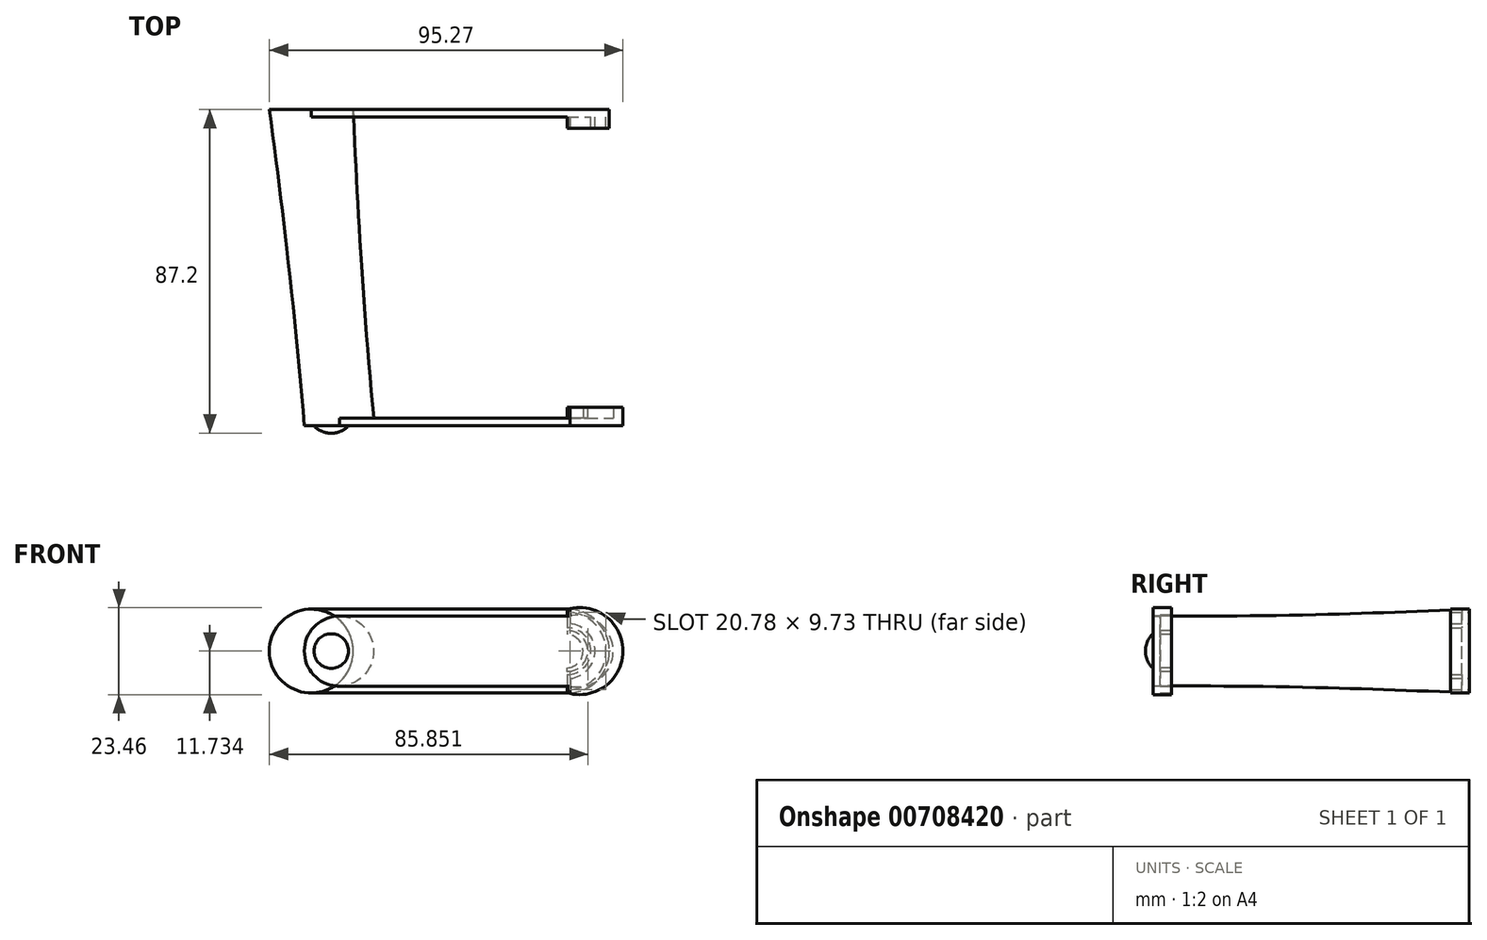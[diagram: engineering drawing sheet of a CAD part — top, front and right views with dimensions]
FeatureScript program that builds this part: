
annotation { "Feature Type Name" : "Feature", "Feature Type Description" : "" }
export const myFeature = defineFeature(function(context is Context, id is Id, definition is map)
    precondition{}
    {
        {
            var Q0;
            Q0=qCreatedBy(makeId("Front.planeOp"),FACE);
            var sketch = newSketch(context, id + "F0", { "sketchPlane" : qUnion([Q0])});
            skCircle(sketch, "E0", {"center": v(0, 0) * mm, "radius": 11.3 * mm});
            skLineSegment(sketch, "E1", {"start": v(0, 11.3) * mm, "end": v(69, 11.3) * mm});
            skLineSegment(sketch, "E2", {"start": v(0, -11.3) * mm, "end": v(69, -11.3) * mm});
            skLineSegment(sketch, "E3", {"start": v(69, 11.3) * mm, "end": v(69, 6.3) * mm});
            skLineSegment(sketch, "E4", {"start": v(69, -6.3) * mm, "end": v(69, -11.3) * mm});
            skArc(sketch, "E5", {"start": v(69, -11.3) * mm, "mid": v(80.3, 0) * mm, "end": v(69, 11.3) * mm});
            skArc(sketch, "E6", {"start": v(69, -6.3) * mm, "mid": v(75.3, 0) * mm, "end": v(69, 6.3) * mm});
            skArc(sketch, "E7", {"start": v(69.69, 10.4) * mm, "mid": v(79.41, 0.06) * mm, "end": v(69.8, -10.38) * mm});
            skArc(sketch, "E8", {"start": v(69.69, 7.4) * mm, "mid": v(76.42, 0.05) * mm, "end": v(69.78, -7.38) * mm});
            skLineSegment(sketch, "E9", {"start": v(69.69, 10.4) * mm, "end": v(69.69, 7.4) * mm});
            skLineSegment(sketch, "E10", {"start": v(69.78, -7.38) * mm, "end": v(69.8, -10.38) * mm});
            skSolve(sketch);
        }
        {
            var Q0;
            Q0=qCreatedBy(makeId("Front.planeOp"),FACE);
            cPlane(context, id + "F1", {"entities" : qUnion([Q0]), "cplaneType" : CPlaneType.OFFSET, "offset" : 85.2 * mm, "width" : 150 * mm, "height" : 150 * mm});
        }
        {
            var Q0;
            Q0=qCreatedBy(id+"F1.planeOp",FACE);
            var sketch = newSketch(context, id + "F2", { "sketchPlane" : qUnion([Q0])});
            skCircle(sketch, "E11", {"center": v(7.55, 0) * mm, "radius": 9.45 * mm});
            skSolve(sketch);
        }
        {
            var Q0;
            Q0=makeQuery(id+"F2.imprint","IMPRINT",FACE,{"disambiguationData":[TD([[makeQuery(id+"F2.imprint","IMPRINT",EDGE,{"derivedFrom":sQuery(id+"F2.wireOp",EDGE,"E11")}),1.0]])]});
            var Q1;
            {var subQ0=sQuery(id+"F0.wireOp",EDGE,"E0");var subQ1=makeQuery(id+"F0.imprint","INTERSECT",VERTEX,{"derivedFrom":[subQ0,sQuery(id+"F0.wireOp",EDGE,"E1")]});Q1=makeQuery(id+"F0.imprint","IMPRINT",FACE,{"disambiguationData":[TD([[makeQuery(id+"F0.imprint","IMPRINT",EDGE,{"disambiguationData":[TD([[subQ1,-1.0]])],"derivedFrom":subQ0}),1.0]])]});}
            loft(context, id + "F3", {"sheetProfilesArray" : [{ "sheetProfileEntities" : qUnion([Q0]) }, { "sheetProfileEntities" : qUnion([Q1]) }]});
        }
        {
            var Q0;
            {var subQ1=sQuery(id+"F0.wireOp",EDGE,"E1");Q0=makeQuery(id+"F0.imprint","IMPRINT",FACE,{"disambiguationData":[TD([[makeQuery(id+"F0.imprint","IMPRINT",EDGE,{"derivedFrom":subQ1}),-1.0]])]});}
            var Q1;
            Q1 = qSketchRegion(id + "F6", true);
            extrude(context, id + "F4", {"entities" : qUnion([Q0, Q1]), "depth" : 2 * mm, "offsetDistance" : 25 * mm});
        }
        {
            var Q0;
            Q0=makeQuery(id+"F0.imprint","IMPRINT",FACE,{"disambiguationData":[TD([[makeQuery(id+"F0.imprint","IMPRINT",EDGE,{"derivedFrom":sQuery(id+"F0.wireOp",EDGE,"E3")}),1.0]])]});
            extrude(context, id + "F5", {"entities" : qUnion([Q0]), "operationType" : NewBodyOperationType.ADD, "depth" : 5 * mm, "offsetDistance" : 25 * mm});
        }
        {
            var Q0;
            Q0=qCreatedBy(id+"F1.planeOp",FACE);
            var sketch = newSketch(context, id + "F6", { "sketchPlane" : qUnion([Q0])});
            skLineSegment(sketch, "E12.bottom", {"start": v(7.55, -9.45) * mm, "end": v(69.67, -9.45) * mm});
            skLineSegment(sketch, "E12.top", {"start": v(7.55, 9.45) * mm, "end": v(69.67, 9.45) * mm});
            skLineSegment(sketch, "E12.left", {"start": v(7.55, -9.45) * mm, "end": v(7.55, 9.45) * mm});
            skArc(sketch, "E13", {"start": v(68.95, -5.5) * mm, "mid": v(74.45, 0) * mm, "end": v(68.95, 5.5) * mm});
            skLineSegment(sketch, "E14", {"start": v(69.67, 9.45) * mm, "end": v(69.67, 11.45) * mm});
            skLineSegment(sketch, "E15", {"start": v(69.67, -9.45) * mm, "end": v(69.67, -11.45) * mm});
            skArc(sketch, "E16", {"start": v(69.67, -11.45) * mm, "mid": v(83.97, 0) * mm, "end": v(69.67, 11.45) * mm});
            skLineSegment(sketch, "E17", {"start": v(68.95, -5.5) * mm, "end": v(68.95, -4.5) * mm});
            skLineSegment(sketch, "E18", {"start": v(68.95, 5.5) * mm, "end": v(68.95, 4.5) * mm});
            skArc(sketch, "E19", {"start": v(68.95, -4.5) * mm, "mid": v(73.2, 0) * mm, "end": v(68.95, 4.5) * mm});
            skArc(sketch, "E20", {"start": v(69.67, -9.45) * mm, "mid": v(81.33, 0) * mm, "end": v(69.67, 9.45) * mm});
            skSolve(sketch);
        }
        {
            var Q0;
            Q0=makeQuery(id+"F6.imprint","IMPRINT",FACE,{"disambiguationData":[TD([[makeQuery(id+"F6.imprint","IMPRINT",EDGE,{"derivedFrom":sQuery(id+"F6.wireOp",EDGE,"E12.bottom")}),1.0]])]});
            extrude(context, id + "F7", {"entities" : qUnion([Q0]), "operationType" : NewBodyOperationType.ADD, "oppositeDirection" : true, "depth" : 2 * mm, "offsetDistance" : 25 * mm});
        }
        {
            var Q0;
            Q0=qCreatedBy(id+"F1.planeOp",FACE);
            var sketch = newSketch(context, id + "F8", { "sketchPlane" : qUnion([Q0])});
            skCircle(sketch, "E21", {"center": v(5.37, 0) * mm, "radius": 4.65 * mm});
            skSolve(sketch);
        }
        {
            var Q0;
            Q0 = qSketchRegion(id + "F8", true);
            extrude(context, id + "F9", {"entities" : qUnion([Q0]), "operationType" : NewBodyOperationType.ADD, "depth" : 2 * mm, "offsetDistance" : 25 * mm});
        }
        {
            var Q0;
            Q0=makeQuery(id+"F9.opExtrude","CAP_FACE",FACE,{"disambiguationData":[OSD([sQuery(id+"F8.wireOp",EDGE,"E21")])],"isStart":false});
            fillet(context, id + "F10", {"entities" : qUnion([Q0]), "radius" : 6 * mm, "tangentPropagation" : true, "allowEdgeOverflow" : false});
        }
        {
            var Q0;
            {var subQ0=sQuery(id+"F6.wireOp",EDGE,"E13");Q0=makeQuery(id+"F6.imprint","IMPRINT",FACE,{"disambiguationData":[TD([[makeQuery(id+"F6.imprint","IMPRINT",EDGE,{"derivedFrom":subQ0}),1.0]])]});}
            extrude(context, id + "F11", {"entities" : qUnion([Q0]), "operationType" : NewBodyOperationType.ADD, "oppositeDirection" : true, "depth" : 2 * mm, "offsetDistance" : 25 * mm});
        }
        {
            var Q0;
            Q0=makeQuery(id+"F0.imprint","IMPRINT",FACE,{"disambiguationData":[TD([[makeQuery(id+"F0.imprint","IMPRINT",EDGE,{"derivedFrom":sQuery(id+"F0.wireOp",EDGE,"E7")}),-1.0]])]});
            extrude(context, id + "F12", {"entities" : qUnion([Q0]), "operationType" : NewBodyOperationType.ADD, "depth" : 2 * mm, "offsetDistance" : 25 * mm});
        }
        {
            var Q0;
            Q0=makeQuery(id+"F0.imprint","IMPRINT",FACE,{"disambiguationData":[TD([[makeQuery(id+"F0.imprint","IMPRINT",EDGE,{"derivedFrom":sQuery(id+"F0.wireOp",EDGE,"E7")}),-1.0]])]});
            extrude(context, id + "F13", {"entities" : qUnion([Q0]), "operationType" : NewBodyOperationType.ADD, "depth" : 3 * mm, "offsetDistance" : 25 * mm});
        }
        {
            var Q0;
            Q0=makeQuery(id+"F6.imprint","IMPRINT",FACE,{"disambiguationData":[TD([[makeQuery(id+"F6.imprint","IMPRINT",EDGE,{"derivedFrom":sQuery(id+"F6.wireOp",EDGE,"E14")}),-1.0]])]});
            extrude(context, id + "F14", {"entities" : qUnion([Q0]), "operationType" : NewBodyOperationType.ADD, "oppositeDirection" : true, "depth" : 5 * mm, "offsetDistance" : 25 * mm});
        }
        {
            var Q0;
            Q0=makeQuery(id+"F6.imprint","IMPRINT",FACE,{"disambiguationData":[TD([[makeQuery(id+"F6.imprint","IMPRINT",EDGE,{"derivedFrom":sQuery(id+"F6.wireOp",EDGE,"E13")}),1.0]])]});
            extrude(context, id + "F15", {"entities" : qUnion([Q0]), "operationType" : NewBodyOperationType.ADD, "oppositeDirection" : true, "depth" : 5 * mm, "offsetDistance" : 25 * mm});
        }
    });
